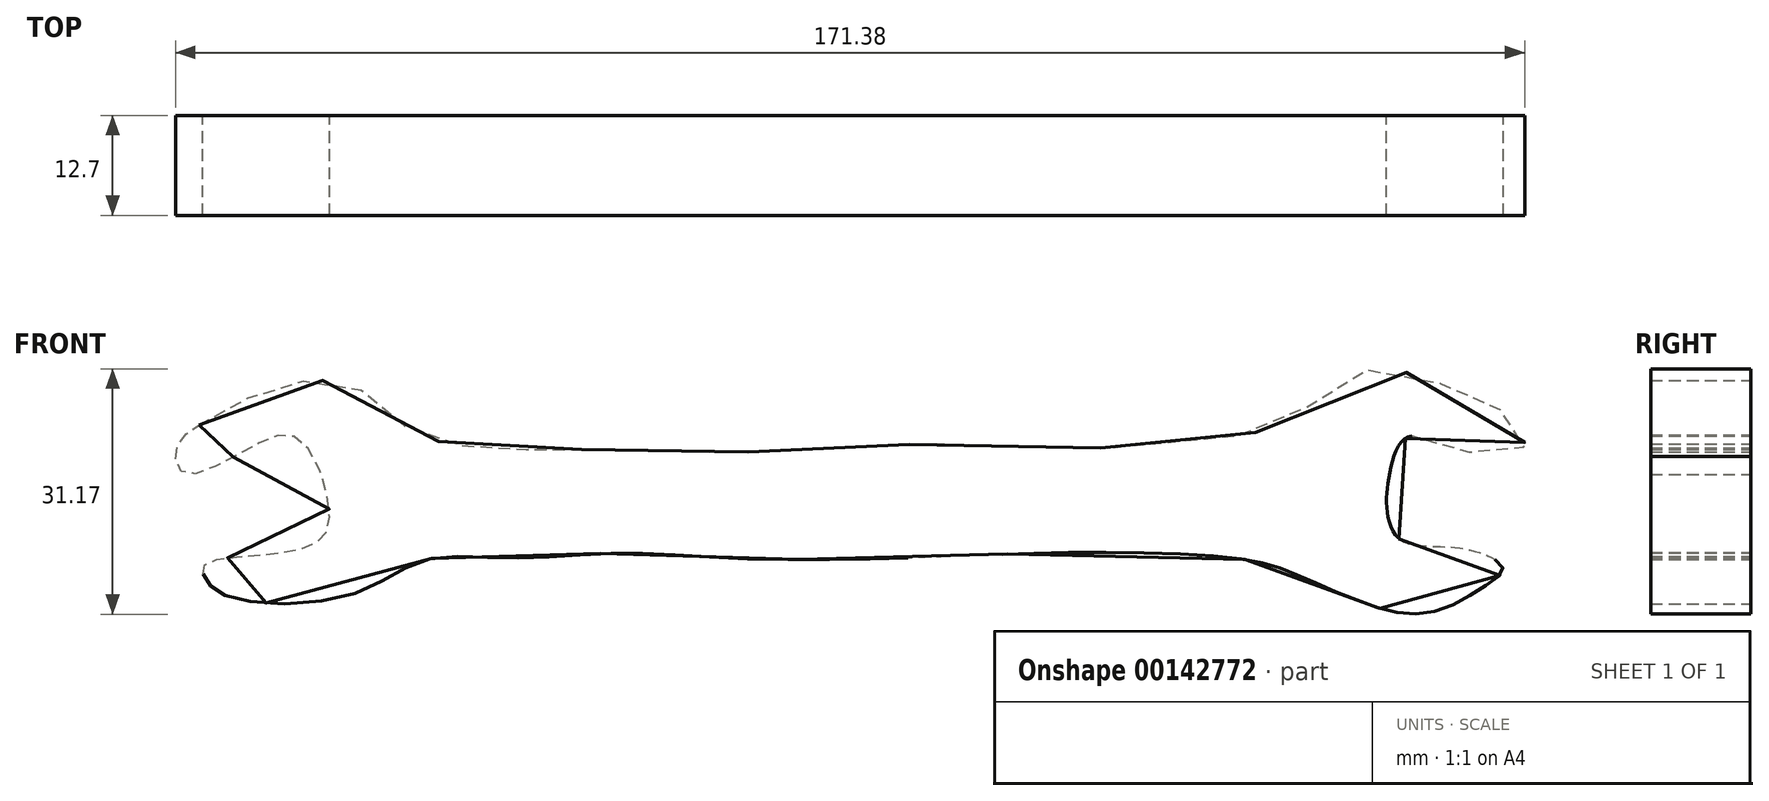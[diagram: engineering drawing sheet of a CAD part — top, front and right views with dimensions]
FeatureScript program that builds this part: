
annotation { "Feature Type Name" : "Feature", "Feature Type Description" : "" }
export const myFeature = defineFeature(function(context is Context, id is Id, definition is map)
    precondition{}
    {
        {
            var Q0;
            Q0=qCreatedBy(makeId("Front.planeOp"),FACE);
            var sketch = newSketch(context, id + "F0", { "sketchPlane" : qUnion([Q0])});
            skLineSegment(sketch, "E0", {"start": v(-47.67, 8.61) * mm, "end": v(53.93, 8.61) * mm});
            skFitSpline(sketch, "E1", {"points": [v(-80.48, 6.1) * mm, v(-74.22, 9.55) * mm, v(-66.7, 11.74) * mm, v(-59.19, 10.18) * mm, v(-53.55, 5.48) * mm, v(-45.1, 3.29) * mm, v(-36.01, 2.97) * mm, v(-27.87, 2.97) * mm, v(-14.4, 2.66) * mm, v(-4.7, 2.97) * mm, v(7.52, 3.6) * mm, v(19.73, 3.6) * mm, v(37.26, 3.29) * mm, v(45.4, 4.23) * mm, v(57.3, 6.42) * mm, v(67.33, 13) * mm, v(79.54, 10.5) * mm, v(86.43, 6.73) * mm, v(87.68, 2.97) * mm, v(79.54, 2.97) * mm, v(72.96, 4.54) * mm, v(70.77, 0) * mm, v(70.46, -4.85) * mm, v(72.34, -8.61) * mm, v(79.85, -9.55) * mm, v(85.18, -12.06) * mm, v(82.98, -14.25) * mm, v(76.1, -17.7) * mm, v(68.27, -16.75) * mm, v(59.19, -13) * mm, v(51.36, -10.8) * mm, v(26, -10.18) * mm, v(8.77, -10.8) * mm, v(-12.84, -10.8) * mm, v(-27.87, -10.18) * mm, v(-40.7, -10.8) * mm, v(-51.98, -11.12) * mm, v(-61.38, -15.5) * mm, v(-76.4, -15.81) * mm, v(-79.54, -13.62) * mm, v(-79.85, -11.74) * mm, v(-73.6, -10.5) * mm, v(-65.76, -8.92) * mm, v(-63.88, -5.48) * mm, v(-67.64, 4.23) * mm, v(-73.9, 3.29) * mm, v(-82.36, 0) * mm, v(-83.3, 3.29) * mm, v(-80.48, 6.1) * mm]});
            skSolve(sketch);
        }
        {
            var Q0;
            Q0=makeQuery(id+"F0.imprint","IMPRINT",FACE,{"disambiguationData":[TD([[makeQuery(id+"F0.imprint","IMPRINT",EDGE,{"derivedFrom":sQuery(id+"F0.wireOp",EDGE,"E1")}),-1.0]])]});
            extrude(context, id + "F1", {"entities" : qUnion([Q0]), "depth" : 12.7 * mm});
        }
    });
